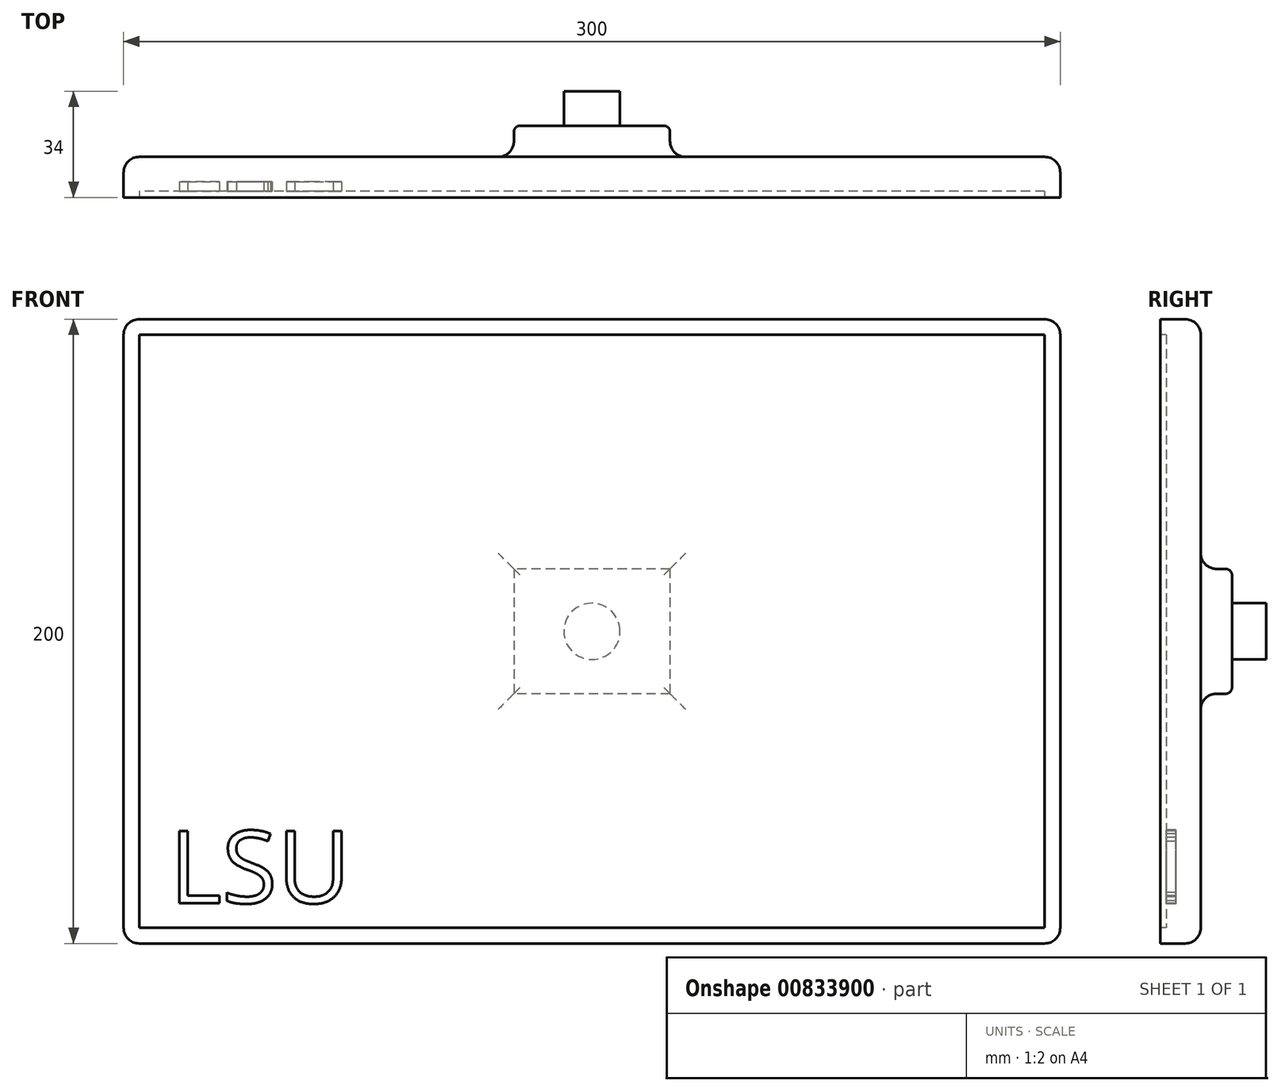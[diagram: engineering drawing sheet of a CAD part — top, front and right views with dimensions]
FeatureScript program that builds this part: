
annotation { "Feature Type Name" : "Feature", "Feature Type Description" : "" }
export const myFeature = defineFeature(function(context is Context, id is Id, definition is map)
    precondition{}
    {
        {
            var Q0;
            Q0=qCreatedBy(makeId("Front.planeOp"),FACE);
            var sketch = newSketch(context, id + "F0", { "sketchPlane" : qUnion([Q0])});
            skLineSegment(sketch, "E0.bottom", {"start": v(-150, 100) * mm, "end": v(150, 100) * mm});
            skLineSegment(sketch, "E0.top", {"start": v(-150, -100) * mm, "end": v(150, -100) * mm});
            skLineSegment(sketch, "E0.left", {"start": v(-150, 100) * mm, "end": v(-150, -100) * mm});
            skLineSegment(sketch, "E0.right", {"start": v(150, 100) * mm, "end": v(150, -100) * mm});
            skSolve(sketch);
        }
        {
            var Q0;
            Q0 = qSketchRegion(id + "F0", true);
            extrude(context, id + "F1", {"entities" : qUnion([Q0]), "endBound" : BoundingType.SYMMETRIC, "depth" : 13 * mm, "offsetDistance" : 25 * mm});
        }
        {
            var Q0;
            Q0=makeQuery(id+"F1.opExtrude","CAP_FACE",FACE,{"disambiguationData":[OSD([sQuery(id+"F0.wireOp",EDGE,"E0.bottom"),sQuery(id+"F0.wireOp",EDGE,"E0.top"),sQuery(id+"F0.wireOp",EDGE,"E0.left"),sQuery(id+"F0.wireOp",EDGE,"E0.right")])],"isStart":false});
            var sketch = newSketch(context, id + "F2", { "sketchPlane" : qUnion([Q0])});
            skLineSegment(sketch, "E1.0", {"start": v(-145, 95) * mm, "end": v(-145, -95) * mm});
            skLineSegment(sketch, "E1.1", {"start": v(145, 95) * mm, "end": v(-145, 95) * mm});
            skLineSegment(sketch, "E1.2", {"start": v(145, -95) * mm, "end": v(145, 95) * mm});
            skLineSegment(sketch, "E1.3", {"start": v(-145, -95) * mm, "end": v(145, -95) * mm});
            skSolve(sketch);
        }
        {
            var Q0;
            Q0=makeQuery(id+"F2.imprint","IMPRINT",FACE,{"disambiguationData":[TD([[makeQuery(id+"F2.imprint","IMPRINT",EDGE,{"derivedFrom":sQuery(id+"F2.wireOp",EDGE,"E1.0")}),1.0]])]});
            extrude(context, id + "F3", {"entities" : qUnion([Q0]), "operationType" : NewBodyOperationType.REMOVE, "oppositeDirection" : true, "depth" : 2 * mm, "offsetDistance" : 25 * mm});
        }
        {
            var Q0;
            Q0=makeQuery(id+"F2.imprint","IMPRINT",FACE,{"disambiguationData":[TD([[makeQuery(id+"F2.imprint","IMPRINT",EDGE,{"derivedFrom":sQuery(id+"F2.wireOp",EDGE,"E1.0")}),1.0]])]});
            var sketch = newSketch(context, id + "F4", { "sketchPlane" : qUnion([Q0])});
            skText(sketch, "E2", { "text": "LSU", "fontName": "OpenSans-Regular.ttf"});
            const initialGuessF4  = {"E2": [-0.13539, -0.08706, 1, 0, 0.0233]};
            skSetInitialGuess(sketch, initialGuessF4);
            skSolve(sketch);
        }
        {
            var Q0;
            Q0 = qSketchRegion(id + "F4", true);
            extrude(context, id + "F5", {"entities" : qUnion([Q0]), "operationType" : NewBodyOperationType.REMOVE, "oppositeDirection" : true, "depth" : 5 * mm, "offsetDistance" : 25 * mm});
        }
        {
            var Q0;
            Q0=makeQuery(id+"F1.opExtrude","CAP_FACE",FACE,{"disambiguationData":[OSD([sQuery(id+"F0.wireOp",EDGE,"E0.bottom"),sQuery(id+"F0.wireOp",EDGE,"E0.top"),sQuery(id+"F0.wireOp",EDGE,"E0.left"),sQuery(id+"F0.wireOp",EDGE,"E0.right")])],"isStart":true});
            var sketch = newSketch(context, id + "F6", { "sketchPlane" : qUnion([Q0])});
            skLineSegment(sketch, "E3.bottom", {"start": v(-25, 20) * mm, "end": v(25, 20) * mm});
            skLineSegment(sketch, "E3.top", {"start": v(-25, -20) * mm, "end": v(25, -20) * mm});
            skLineSegment(sketch, "E3.left", {"start": v(-25, 20) * mm, "end": v(-25, -20) * mm});
            skLineSegment(sketch, "E3.right", {"start": v(25, 20) * mm, "end": v(25, -20) * mm});
            skSolve(sketch);
        }
        {
            var Q0;
            Q0=makeQuery(id+"F6.imprint","IMPRINT",FACE,{"disambiguationData":[TD([[makeQuery(id+"F6.imprint","IMPRINT",EDGE,{"derivedFrom":sQuery(id+"F6.wireOp",EDGE,"E3.bottom")}),-1.0]])]});
            extrude(context, id + "F7", {"entities" : qUnion([Q0]), "operationType" : NewBodyOperationType.ADD, "depth" : 10 * mm, "offsetDistance" : 25 * mm});
        }
        {
            var Q0;
            Q0=makeQuery(id+"F7.opExtrude","CAP_FACE",FACE,{"disambiguationData":[OSD([sQuery(id+"F6.wireOp",EDGE,"E3.bottom"),sQuery(id+"F6.wireOp",EDGE,"E3.top"),sQuery(id+"F6.wireOp",EDGE,"E3.left"),sQuery(id+"F6.wireOp",EDGE,"E3.right")])],"isStart":false});
            var sketch = newSketch(context, id + "F8", { "sketchPlane" : qUnion([Q0])});
            skCircle(sketch, "E4", {"center": v(0, 0) * mm, "radius": 9 * mm});
            skSolve(sketch);
        }
        {
            var Q0;
            Q0 = qSketchRegion(id + "F8", true);
            extrude(context, id + "F9", {"entities" : qUnion([Q0]), "operationType" : NewBodyOperationType.ADD, "depth" : 11 * mm, "offsetDistance" : 25 * mm});
        }
        {
            var Q0;
            Q0=makeQuery(id+"F7.opExtrude","CAP_EDGE",EDGE,{"disambiguationData":[OSD([sQuery(id+"F6.wireOp",EDGE,"E3.left")])],"isStart":true});
            var Q1;
            Q1=makeQuery(id+"F7.opExtrude","CAP_EDGE",EDGE,{"disambiguationData":[OSD([sQuery(id+"F6.wireOp",EDGE,"E3.bottom")])],"isStart":true});
            var Q2;
            Q2=makeQuery(id+"F7.opExtrude","CAP_EDGE",EDGE,{"disambiguationData":[OSD([sQuery(id+"F6.wireOp",EDGE,"E3.top")])],"isStart":true});
            var Q3;
            Q3=makeQuery(id+"F7.opExtrude","CAP_EDGE",EDGE,{"disambiguationData":[OSD([sQuery(id+"F6.wireOp",EDGE,"E3.right")])],"isStart":true});
            var Q4;
            Q4=makeQuery(id+"F7.opExtrude","CAP_EDGE",EDGE,{"disambiguationData":[OSD([sQuery(id+"F6.wireOp",EDGE,"E3.right")])],"isStart":false});
            var Q5;
            Q5=makeQuery(id+"F7.opExtrude","CAP_EDGE",EDGE,{"disambiguationData":[OSD([sQuery(id+"F6.wireOp",EDGE,"E3.top")])],"isStart":false});
            var Q6;
            Q6=makeQuery(id+"F7.opExtrude","CAP_EDGE",EDGE,{"disambiguationData":[OSD([sQuery(id+"F6.wireOp",EDGE,"E3.left")])],"isStart":false});
            var Q7;
            Q7=makeQuery(id+"F7.opExtrude","CAP_EDGE",EDGE,{"disambiguationData":[OSD([sQuery(id+"F6.wireOp",EDGE,"E3.bottom")])],"isStart":false});
            fillet(context, id + "F10", {"entities" : qUnion([Q0, Q1, Q2, Q3, Q4, Q5, Q6, Q7]), "radius" : 2 * mm, "tangentPropagation" : true, "allowEdgeOverflow" : false});
        }
        {
            var Q0;
            Q0=makeQuery(id+"F1.opExtrude","CAP_FACE",FACE,{"disambiguationData":[OSD([sQuery(id+"F0.wireOp",EDGE,"E0.bottom"),sQuery(id+"F0.wireOp",EDGE,"E0.top"),sQuery(id+"F0.wireOp",EDGE,"E0.left"),sQuery(id+"F0.wireOp",EDGE,"E0.right")])],"isStart":true});
            var Q1;
            Q1=makeQuery(id+"F1.opExtrude","SWEPT_EDGE",EDGE,{"disambiguationData":[OSD([sQuery(id+"F0.wireOp",EDGE,"E0.top"),sQuery(id+"F0.wireOp",EDGE,"E0.left")])]});
            var Q2;
            Q2=makeQuery(id+"F1.opExtrude","SWEPT_EDGE",EDGE,{"disambiguationData":[OSD([sQuery(id+"F0.wireOp",EDGE,"E0.bottom"),sQuery(id+"F0.wireOp",EDGE,"E0.left")])]});
            var Q3;
            Q3=makeQuery(id+"F1.opExtrude","SWEPT_EDGE",EDGE,{"disambiguationData":[OSD([sQuery(id+"F0.wireOp",EDGE,"E0.bottom"),sQuery(id+"F0.wireOp",EDGE,"E0.right")])]});
            var Q4;
            Q4=makeQuery(id+"F1.opExtrude","SWEPT_EDGE",EDGE,{"disambiguationData":[OSD([sQuery(id+"F0.wireOp",EDGE,"E0.top"),sQuery(id+"F0.wireOp",EDGE,"E0.right")])]});
            fillet(context, id + "F11", {"entities" : qUnion([Q0, Q1, Q2, Q3, Q4]), "radius" : 5 * mm, "tangentPropagation" : true, "allowEdgeOverflow" : false});
        }
    });
